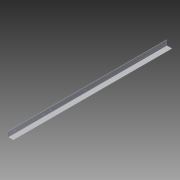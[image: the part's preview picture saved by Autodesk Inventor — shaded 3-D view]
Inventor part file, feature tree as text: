
AUTODESK INVENTOR PART (.ipt)
format: ipt  version: 2014 SP1 (Build 180222100, 222)  size: 98,304 bytes
history: native  units: in
note: dims shown in document units (in); Inventor stores cm internally (conversion verified against a paired STEP export)
features: reference x3, extrude x2, sketch x2
ambient origin geometry x8: Origin, YZ Plane, XZ Plane, XY Plane, X Axis, Y Axis, Z Axis, Center Point
bodies: Solid1 (feature_tree)
feature tree (7):
  extrude  "Extrusion1"  Depth=0.0312in
  extrude  "Extrusion2"  Depth=18.688in TaperAngle=0.0deg
  sketch  "Sketch1"  dims[d0=0.625in d1=0.0312in]
  sketch  "Sketch2"  dims[d2=0.0312in d3=18.688in d4=0.0in d5=0.177in d8=0.75in d9=5.0in d10=9.0in d11=0.25in d12=3.25in d13=1.0in d14=0.0in]
  reference  "Reference1"
  reference  "Reference2"
  reference  "Reference3"
